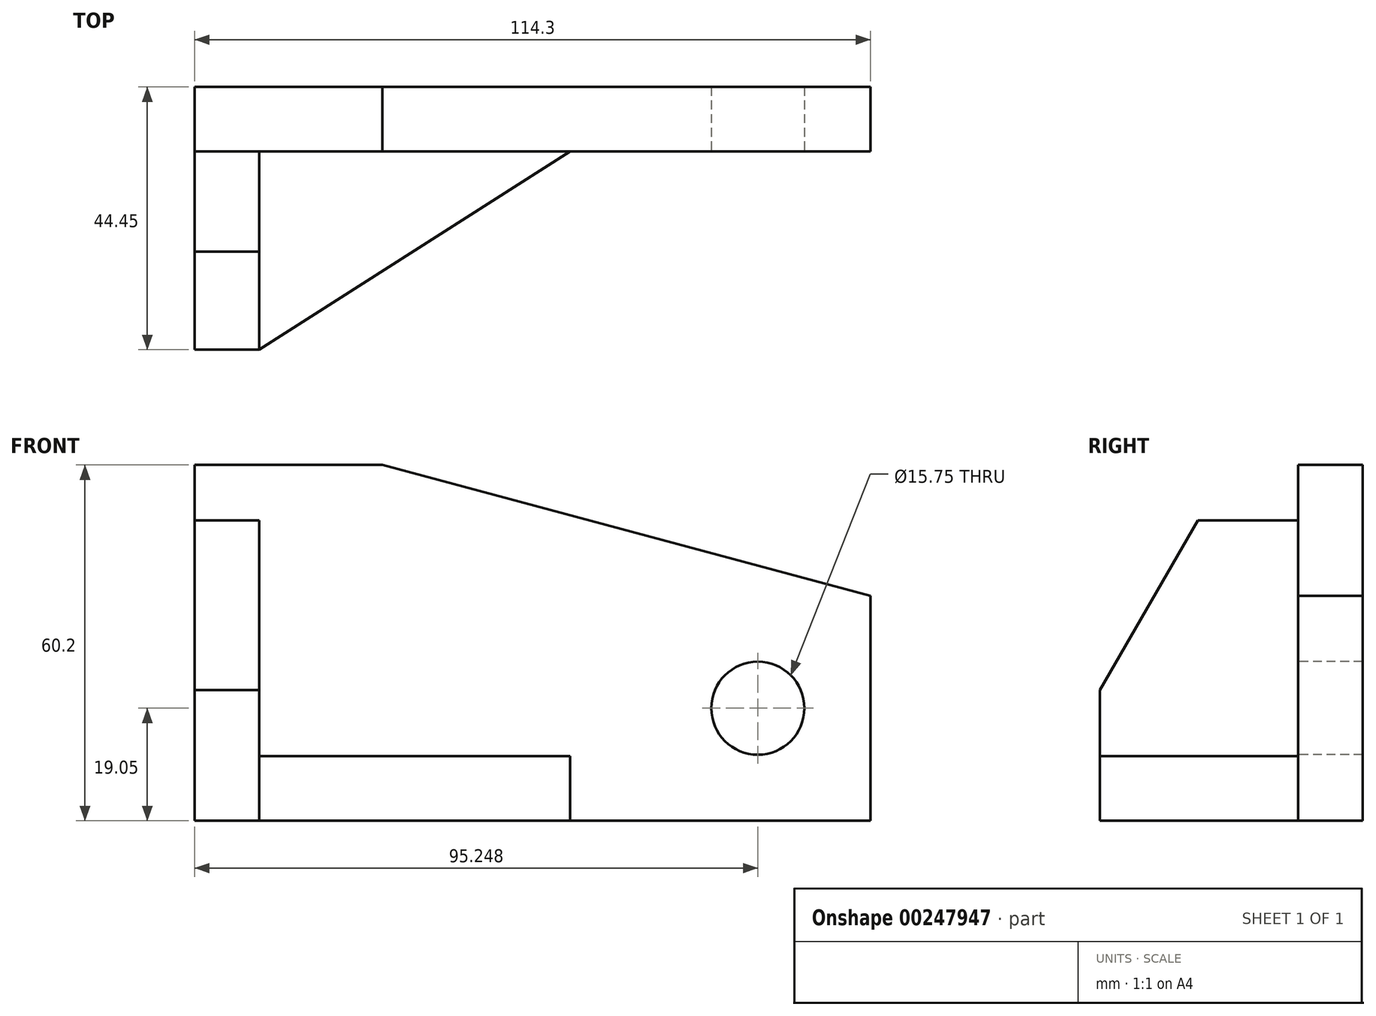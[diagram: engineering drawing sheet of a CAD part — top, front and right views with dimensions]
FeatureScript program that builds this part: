
annotation { "Feature Type Name" : "Feature", "Feature Type Description" : "" }
export const myFeature = defineFeature(function(context is Context, id is Id, definition is map)
    precondition{}
    {
        {
            var Q0;
            Q0=qCreatedBy(makeId("Front.planeOp"),FACE);
            var sketch = newSketch(context, id + "F0", { "sketchPlane" : qUnion([Q0])});
            skLineSegment(sketch, "E0", {"start": v(0, 0) * mm, "end": v(-10.92, 0) * mm});
            skLineSegment(sketch, "E1", {"start": v(-10.92, 0) * mm, "end": v(-10.92, 60.2) * mm});
            skLineSegment(sketch, "E2", {"start": v(-10.92, 60.2) * mm, "end": v(20.83, 60.2) * mm});
            skLineSegment(sketch, "E3", {"start": v(103.38, 38.08) * mm, "end": v(103.38, 0) * mm});
            skLineSegment(sketch, "E4", {"start": v(103.38, 0) * mm, "end": v(0, 0) * mm});
            skLineSegment(sketch, "E5", {"start": v(20.83, 60.2) * mm, "end": v(103.38, 38.08) * mm});
            skCircle(sketch, "E6", {"center": v(84.33, 19.05) * mm, "radius": 7.87 * mm});
            skSolve(sketch);
        }
        {
            var Q0;
            Q0 = qSketchRegion(id + "F0", true);
            extrude(context, id + "F1", {"entities" : qUnion([Q0]), "oppositeDirection" : true, "depth" : 10.92 * mm});
        }
        {
            var Q0;
            Q0=qCreatedBy(makeId("Right.planeOp"),FACE);
            var sketch = newSketch(context, id + "F2", { "sketchPlane" : qUnion([Q0])});
            skLineSegment(sketch, "E7", {"start": v(0, 0) * mm, "end": v(-33.53, 0) * mm});
            skLineSegment(sketch, "E8", {"start": v(-33.53, 0) * mm, "end": v(-33.53, 22.1) * mm});
            skLineSegment(sketch, "E9", {"start": v(-33.53, 22.1) * mm, "end": v(-16.96, 50.8) * mm});
            skLineSegment(sketch, "E10", {"start": v(-16.96, 50.8) * mm, "end": v(0, 50.8) * mm});
            skLineSegment(sketch, "E11", {"start": v(0, 50.8) * mm, "end": v(0, 0) * mm});
            skSolve(sketch);
        }
        {
            var Q0;
            Q0 = qSketchRegion(id + "F2", true);
            extrude(context, id + "F3", {"entities" : qUnion([Q0]), "operationType" : NewBodyOperationType.ADD, "oppositeDirection" : true, "depth" : 10.92 * mm});
        }
        {
            var Q0;
            Q0=qCreatedBy(makeId("Top.planeOp"),FACE);
            var sketch = newSketch(context, id + "F4", { "sketchPlane" : qUnion([Q0])});
            skLineSegment(sketch, "E12", {"start": v(0, 0) * mm, "end": v(52.58, 0) * mm});
            skLineSegment(sketch, "E13", {"start": v(52.58, 0) * mm, "end": v(0, -33.53) * mm});
            skLineSegment(sketch, "E14", {"start": v(0, -33.53) * mm, "end": v(0, 0) * mm});
            skSolve(sketch);
        }
        {
            var Q0;
            Q0 = qSketchRegion(id + "F4", true);
            extrude(context, id + "F5", {"entities" : qUnion([Q0]), "operationType" : NewBodyOperationType.ADD, "depth" : 10.92 * mm});
        }
    });
